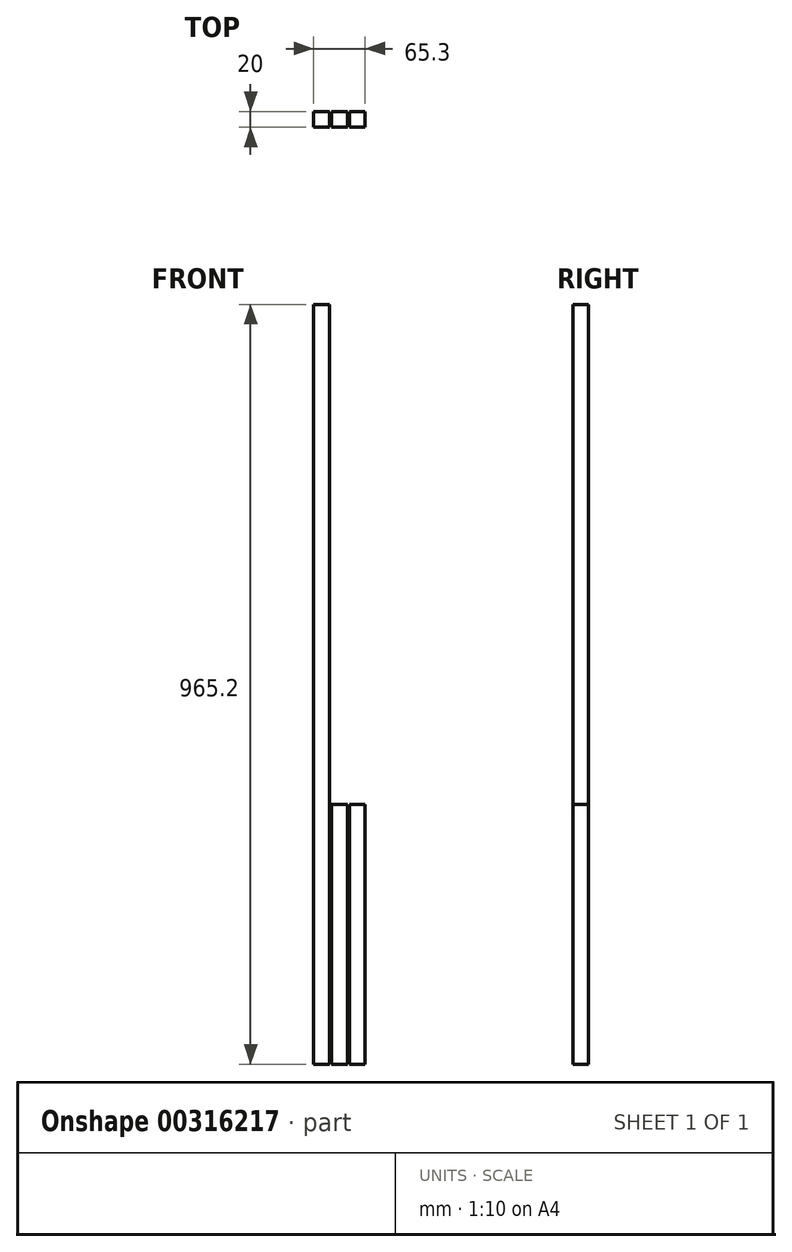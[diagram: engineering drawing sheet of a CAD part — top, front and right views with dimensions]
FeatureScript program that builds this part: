
annotation { "Feature Type Name" : "Feature", "Feature Type Description" : "" }
export const myFeature = defineFeature(function(context is Context, id is Id, definition is map)
    precondition{}
    {
        {
            assignVariable(context, id + "F0", {"name" : "batteries", "anyValue" : 10});
        }
        {
            assignVariable(context, id + "F1", {"name" : "battery_thickness", "anyValue" : 76.2 * mm});
        }
        {
            assignVariable(context, id + "F2", {"name" : "battery_slot_width", "anyValue" : 203.2 * mm});
        }
        {
            assignVariable(context, id + "F3", {"name" : "depth", "anyValue" : 330.2 * mm});
        }
        {
            var Q0;
            Q0=qCreatedBy(makeId("Top.planeOp"),FACE);
            var sketch = newSketch(context, id + "F4", { "sketchPlane" : qUnion([Q0])});
            skLineSegment(sketch, "E0.bottom", {"start": v(-92.78, 35.81) * mm, "end": v(-72.78, 35.81) * mm});
            skLineSegment(sketch, "E0.top", {"start": v(-92.78, 15.81) * mm, "end": v(-72.78, 15.81) * mm});
            skLineSegment(sketch, "E0.left", {"start": v(-92.78, 35.81) * mm, "end": v(-92.78, 15.81) * mm});
            skLineSegment(sketch, "E0.right", {"start": v(-72.78, 35.81) * mm, "end": v(-72.78, 15.81) * mm});
            skPoint(sketch, "E0.middle", {"position": v(-82.78, 25.81) * mm});
            skLineSegment(sketch, "E1.bottom", {"start": v(-50.13, 15.81) * mm, "end": v(-70.13, 15.81) * mm});
            skLineSegment(sketch, "E1.top", {"start": v(-50.13, 35.81) * mm, "end": v(-70.13, 35.81) * mm});
            skLineSegment(sketch, "E1.left", {"start": v(-50.13, 15.81) * mm, "end": v(-50.13, 35.81) * mm});
            skLineSegment(sketch, "E1.right", {"start": v(-70.13, 15.81) * mm, "end": v(-70.13, 35.81) * mm});
            skPoint(sketch, "E1.middle", {"position": v(-60.13, 25.81) * mm});
            skLineSegment(sketch, "E2.bottom", {"start": v(-27.48, 15.81) * mm, "end": v(-47.48, 15.81) * mm});
            skLineSegment(sketch, "E2.top", {"start": v(-27.48, 35.81) * mm, "end": v(-47.48, 35.81) * mm});
            skLineSegment(sketch, "E2.left", {"start": v(-27.48, 15.81) * mm, "end": v(-27.48, 35.81) * mm});
            skLineSegment(sketch, "E2.right", {"start": v(-47.48, 15.81) * mm, "end": v(-47.48, 35.81) * mm});
            skPoint(sketch, "E2.middle", {"position": v(-37.48, 25.81) * mm});
            skLineSegment(sketch, "E3", {"start": v(-82.78, 25.81) * mm, "end": v(-37.48, 25.81) * mm, "construction": true});
            skSolve(sketch);
        }
        {
            var Q0;
            Q0=makeQuery(id+"F4.imprint","IMPRINT",FACE,{"disambiguationData":[TD([[makeQuery(id+"F4.imprint","IMPRINT",EDGE,{"derivedFrom":sQuery(id+"F4.wireOp",EDGE,"E0.bottom")}),-1.0]])]});
            extrude(context, id + "F5", {"entities" : qUnion([Q0]), "depth" : getVariable(context, 'batteries') * getVariable(context, 'battery_thickness') + 203.2 * mm});
        }
        {
            var Q0;
            Q0=makeQuery(id+"F4.imprint","IMPRINT",FACE,{"disambiguationData":[TD([[makeQuery(id+"F4.imprint","IMPRINT",EDGE,{"derivedFrom":sQuery(id+"F4.wireOp",EDGE,"E1.bottom")}),-1.0]])]});
            extrude(context, id + "F6", {"entities" : qUnion([Q0]), "depth" : getVariable(context, 'battery_slot_width') + 127 * mm});
        }
        {
            var Q0;
            Q0=makeQuery(id+"F4.imprint","IMPRINT",FACE,{"disambiguationData":[TD([[makeQuery(id+"F4.imprint","IMPRINT",EDGE,{"derivedFrom":sQuery(id+"F4.wireOp",EDGE,"E2.bottom")}),-1.0]])]});
            extrude(context, id + "F7", {"entities" : qUnion([Q0]), "depth" : getVariable(context, 'depth')});
        }
    });
